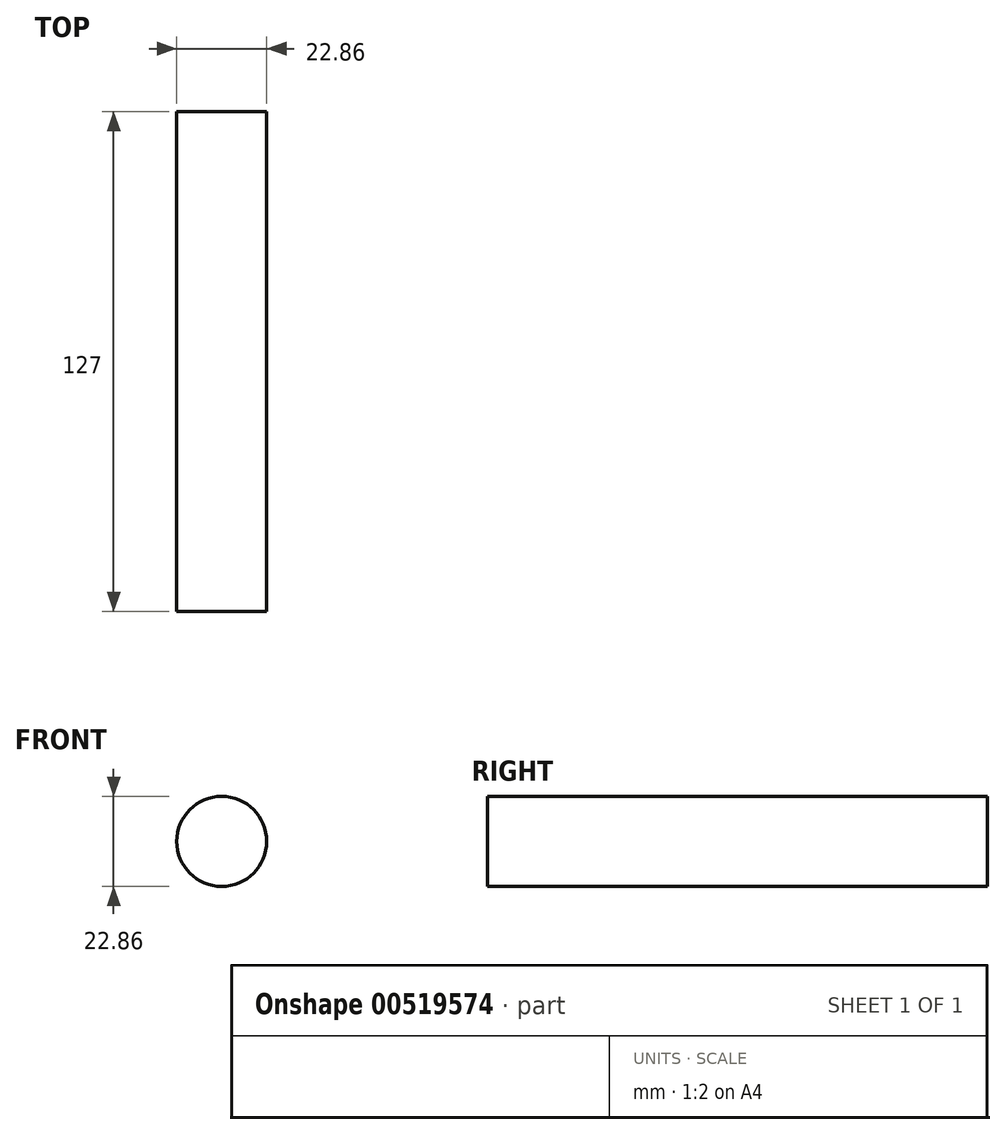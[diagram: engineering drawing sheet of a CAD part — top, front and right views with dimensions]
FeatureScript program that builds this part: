
annotation { "Feature Type Name" : "Feature", "Feature Type Description" : "" }
export const myFeature = defineFeature(function(context is Context, id is Id, definition is map)
    precondition{}
    {
        {
            var Q0;
            Q0=qCreatedBy(makeId("Front.planeOp"),FACE);
            var sketch = newSketch(context, id + "F0", { "sketchPlane" : qUnion([Q0])});
            skCircle(sketch, "E0", {"center": v(0, 0) * mm, "radius": 11.43 * mm});
            skPoint(sketch, "E1.orphan", {"position": v(-11.43, 0) * mm});
            skSolve(sketch);
        }
        {
            var Q0;
            {var subQ0=sQuery(id+"F0.wireOp",EDGE,"j1OS6oN0-YWDv-fQow-mlOw-UQIUOfXuzx5P");Q0=makeQuery(id+"F0.imprint","IMPRINT",FACE,{"disambiguationData":[TD([[makeQuery(id+"F0.imprint","IMPRINT",EDGE,{"derivedFrom":subQ0}),-1.0]])]});}
            var Q1;
            {var subQ0=sQuery(id+"F0.wireOp",EDGE,"j1OS6oN0-YWDv-fQow-mlOw-UQIUOfXuzx5P");Q1=makeQuery(id+"F0.imprint","IMPRINT",FACE,{"disambiguationData":[TD([[makeQuery(id+"F0.imprint","IMPRINT",EDGE,{"derivedFrom":subQ0}),1.0]])]});}
            var Q2;
            Q2=makeQuery(id+"F0.imprint","IMPRINT",FACE,{"disambiguationData":[TD([[makeQuery(id+"F0.imprint","IMPRINT",EDGE,{"derivedFrom":sQuery(id+"F0.wireOp",EDGE,"E0")}),1.0]])]});
            extrude(context, id + "F1", {"entities" : qUnion([Q0, Q1, Q2]), "depth" : 127 * mm, "offsetDistance" : 25.4 * mm});
        }
    });
